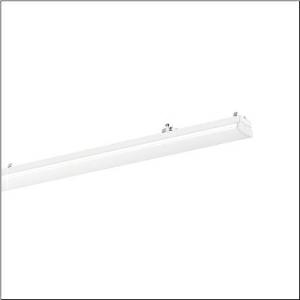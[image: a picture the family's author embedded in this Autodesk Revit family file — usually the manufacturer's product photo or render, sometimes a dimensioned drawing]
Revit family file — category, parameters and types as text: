
# Revit family: licross_r__11_recessed_opal_mo_51tl1ddn46xg_c64a
name_source: partatom
category: Lighting Fixtures
units: mm (PartAtom-declared; Revit-internal decimal feet)

## family parameters
Cut with Voids When Loaded = No
Host = Face
Light Source = No
Part Type = Normal
Room Calculation Point = No
Round Connector Dimension = Use Diameter
Shared = No

## types (1)
- --- (1 x LED, 6320 lm, 35.2 W, 4000K)
    Apparent Load = 35 VA
    CIE Flux Codes = 44 73 91 87 100
    Color Rendering = 80
    Color Temperature = 4000K
    Default Elevation = 1800 mm
    Description = Licross® 11 recessed opal MO, luminaire insert, of sheet steel, coil coated, white, length: 1.500mm, width: 76mm, height: 87mm, LED rated luminous flux: 6.320lm, light colour: 840, control gear: DALI 2, with plug, 5-pole, with phase selection, mains connection: 220..240V, AC, 50/60Hz, rated input power: 35W, internal wiring halogen-free, primary optical cover: cover, of PMMA, light emission: direct with ceiling illumination distribution, primary light characteristic: symmetric, protection rating (complete): IP40, insulation class (complete): insulation class I (protective earthing), certification: CE, ENEC, VDE, UKCA, protection symbol: D if used in an environment without relevant dust loads with corresponding accessories, impact resistance: IK06, permissible ambient temperature for indoor applications: -25..+40°C, corresponds to IFS (International Featured Standards) requirements for safety and quality in the food industry, reducing of maximum allowable ambient temperature of 5°C with ceiling mounting, LABS conformity tested according to VDMA 24364:2018-05, packaging unit: 1 piece
    Height = 83 mm
    Lamp = 1 x LED
    Lamp Light Flux = 6320 lm
    Lamp Power = 35.2 W
    Lamp count = 1
    Length = 1500 mm
    Luminous efficacy = 180 lm/W
    Manufacturer = Siteco
    ModVariant = No
    Model = 51TL1DDN46XG
    Mounting Place = Ceiling
    Mounting Type = Pendant
    Number of Poles = 1
    OnlyDefault = Yes
    Power Factor = 1
    Product Name = Licross® 11 recessed opal MO
    Product group = luminaire insert | ceiling pendant
    ProductGroupID = 902
    Protection Class = Protection class I
    Protection Degree = IP 40
    RLX_Detail_Level = 1
    RLX_Emergency_Light_Flux = 0 lm
    RLX_Emergency_Type = 0
    RLX_Emergency_Type_DB = No
    RlxData = <blob elided: 26817 chars, md5=4975aea3>
    Socket = socket
    Standby Power = 0 W
    System Light Flux = 6320 lm
    System Power = 35 W
    Type Comments = factory setting: luminous flux: 100 % | dim-lin: 254 | 238 mA
    Type Image = l_1313666.jpg
    URL = http://relux.com
    VarID = @adj_097713
    Voltage = 0 V
    Weight = 0.00 kg
    Width = 76 mm

## geometry (parser evidence)
native form markers: Blend x4, Sweep x13
no freeform markers — native parametric forms only
